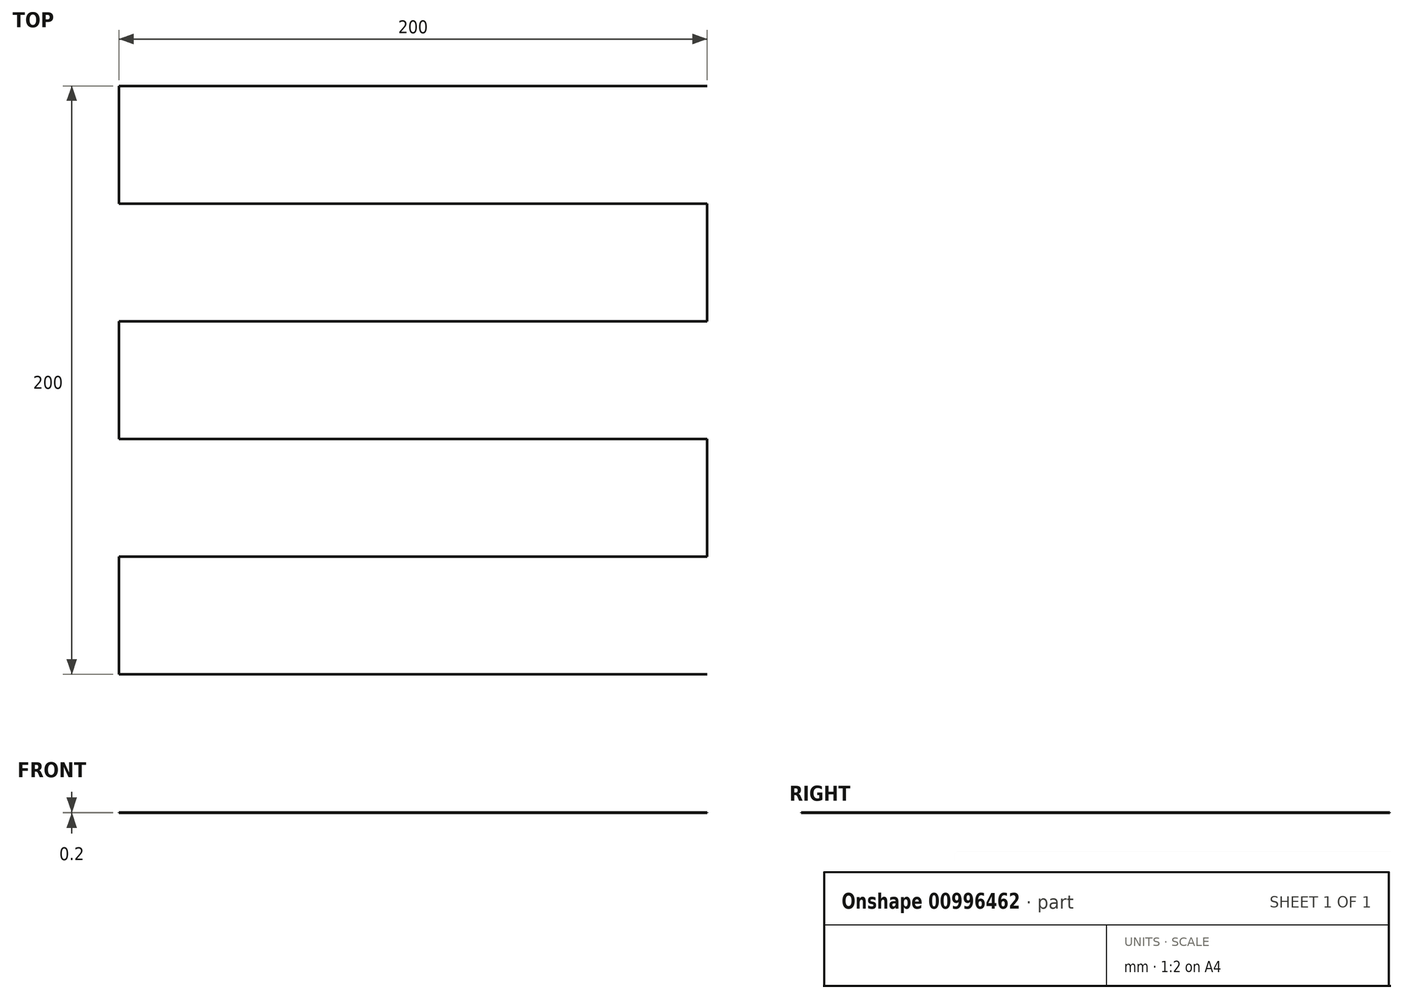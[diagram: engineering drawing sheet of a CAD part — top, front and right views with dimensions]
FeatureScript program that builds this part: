
annotation { "Feature Type Name" : "Feature", "Feature Type Description" : "" }
export const myFeature = defineFeature(function(context is Context, id is Id, definition is map)
    precondition{}
    {
        {
            var Q0;
            Q0=qCreatedBy(makeId("Top.planeOp"),FACE);
            var sketch = newSketch(context, id + "F0", { "sketchPlane" : qUnion([Q0])});
            skLineSegment(sketch, "E0.bottom", {"start": v(98, 58.2) * mm, "end": v(-102, 58.2) * mm, "construction": true});
            skLineSegment(sketch, "E0.top", {"start": v(98, 18.2) * mm, "end": v(-102, 18.2) * mm, "construction": true});
            skLineSegment(sketch, "E0.left", {"start": v(98, 58.2) * mm, "end": v(98, 18.2) * mm, "construction": true});
            skLineSegment(sketch, "E0.right", {"start": v(-102, 58.2) * mm, "end": v(-102, 18.2) * mm, "construction": true});
            skLineSegment(sketch, "E1.bottom", {"start": v(98, -21.8) * mm, "end": v(-102, -21.8) * mm, "construction": true});
            skLineSegment(sketch, "E1.top", {"start": v(98, -61.8) * mm, "end": v(-102, -61.8) * mm, "construction": true});
            skLineSegment(sketch, "E1.left", {"start": v(98, -21.8) * mm, "end": v(98, -61.8) * mm, "construction": true});
            skLineSegment(sketch, "E1.right", {"start": v(-102, -21.8) * mm, "end": v(-102, -61.8) * mm, "construction": true});
            skLineSegment(sketch, "E2.bottom", {"start": v(98, -101.8) * mm, "end": v(-102, -101.8) * mm, "construction": true});
            skLineSegment(sketch, "E2.top", {"start": v(98, -141.8) * mm, "end": v(-102, -141.8) * mm, "construction": true});
            skLineSegment(sketch, "E2.left", {"start": v(98, -101.8) * mm, "end": v(98, -141.8) * mm, "construction": true});
            skLineSegment(sketch, "E2.right", {"start": v(-102, -101.8) * mm, "end": v(-102, -141.8) * mm, "construction": true});
            skLineSegment(sketch, "E3", {"start": v(98, 58.2) * mm, "end": v(-102, 58.2) * mm});
            skLineSegment(sketch, "E4", {"start": v(-102, 58.2) * mm, "end": v(-102, 18.2) * mm});
            skLineSegment(sketch, "E5", {"start": v(-102, 18.2) * mm, "end": v(98, 18.2) * mm});
            skLineSegment(sketch, "E6", {"start": v(98, 18.2) * mm, "end": v(98, -21.8) * mm});
            skLineSegment(sketch, "E7", {"start": v(98, -21.8) * mm, "end": v(-102, -21.8) * mm});
            skLineSegment(sketch, "E8", {"start": v(-102, -21.8) * mm, "end": v(-102, -61.8) * mm});
            skLineSegment(sketch, "E9", {"start": v(-102, -61.8) * mm, "end": v(98, -61.8) * mm});
            skLineSegment(sketch, "E10", {"start": v(98, -61.8) * mm, "end": v(98, -101.8) * mm});
            skLineSegment(sketch, "E11", {"start": v(98, -101.8) * mm, "end": v(-102, -101.8) * mm});
            skLineSegment(sketch, "E12", {"start": v(-102, -101.8) * mm, "end": v(-102, -141.8) * mm});
            skLineSegment(sketch, "E13", {"start": v(-102, -141.8) * mm, "end": v(98, -141.8) * mm});
            skSolve(sketch);
        }
        {
            var Q0;
            Q0=sQuery(id+"F0.wireOp",EDGE,"E11");
            var Q1;
            Q1=sQuery(id+"F0.wireOp",EDGE,"E12");
            var Q2;
            Q2=sQuery(id+"F0.wireOp",EDGE,"E13");
            var Q3;
            Q3=sQuery(id+"F0.wireOp",EDGE,"E10");
            var Q4;
            Q4=sQuery(id+"F0.wireOp",EDGE,"E9");
            var Q5;
            Q5=sQuery(id+"F0.wireOp",EDGE,"E8");
            var Q6;
            Q6=sQuery(id+"F0.wireOp",EDGE,"E7");
            var Q7;
            Q7=sQuery(id+"F0.wireOp",EDGE,"E6");
            var Q8;
            Q8=sQuery(id+"F0.wireOp",EDGE,"E5");
            var Q9;
            Q9=sQuery(id+"F0.wireOp",EDGE,"E4");
            var Q10;
            Q10=sQuery(id+"F0.wireOp",EDGE,"E3");
            extrude(context, id + "F1", {"bodyType" : ToolBodyType.SURFACE, "surfaceEntities" : qUnion([Q0, Q1, Q2, Q3, Q4, Q5, Q6, Q7, Q8, Q9, Q10]), "depth" : 0.2 * mm, "offsetDistance" : 25 * mm});
        }
    });
